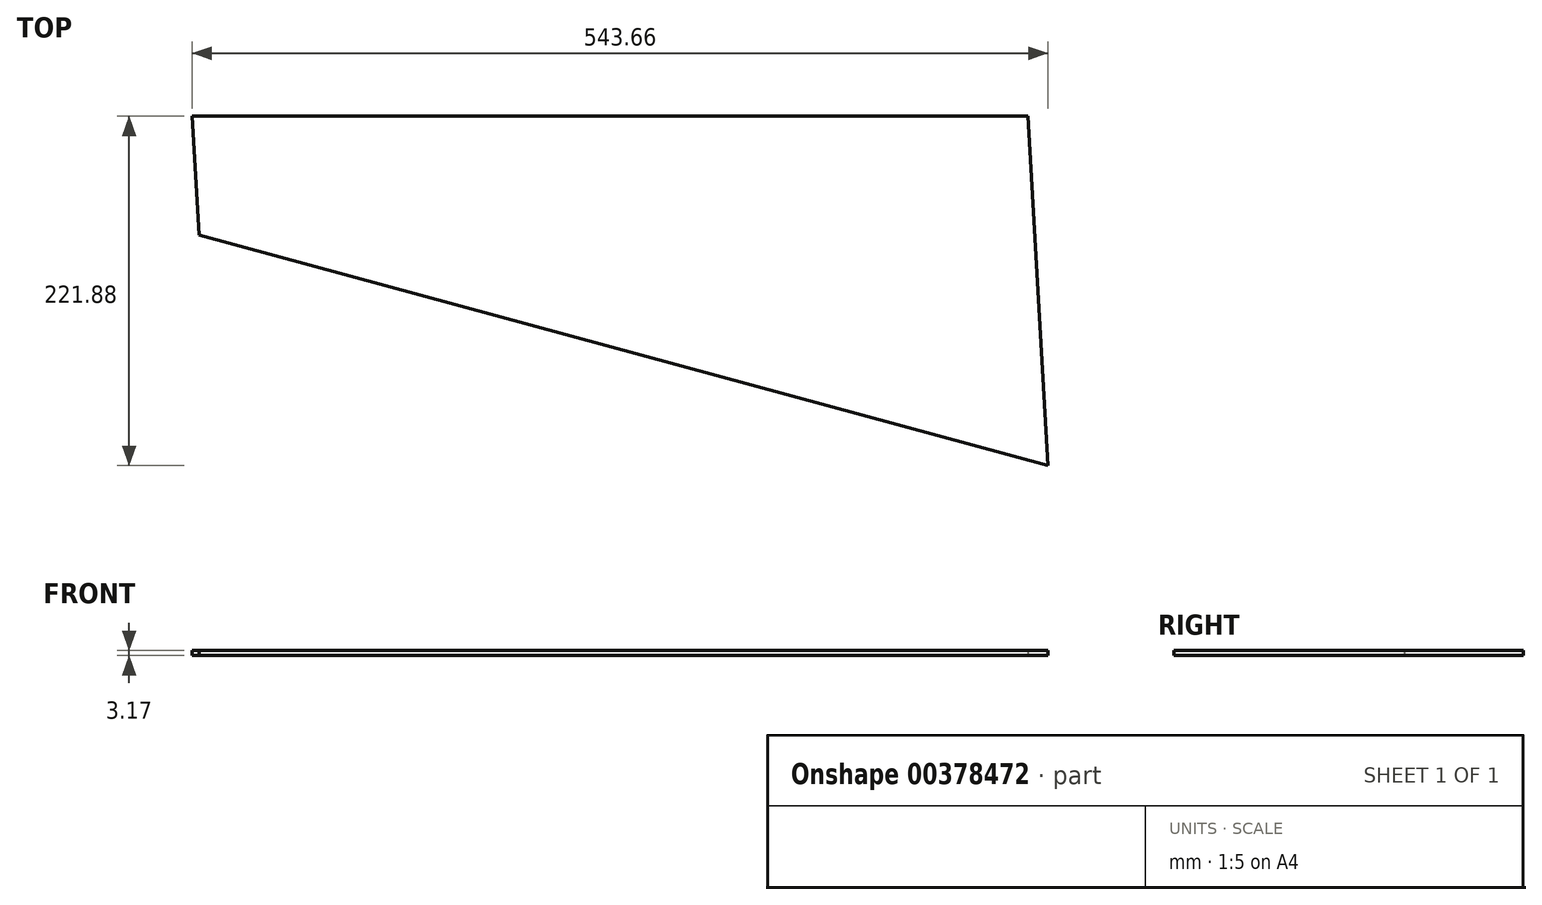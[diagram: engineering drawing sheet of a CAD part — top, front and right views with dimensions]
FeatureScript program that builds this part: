
annotation { "Feature Type Name" : "Feature", "Feature Type Description" : "" }
export const myFeature = defineFeature(function(context is Context, id is Id, definition is map)
    precondition{}
    {
        {
            var Q0;
            Q0=qCreatedBy(makeId("Top.planeOp"),FACE);
            var sketch = newSketch(context, id + "F0", { "sketchPlane" : qUnion([Q0])});
            skLineSegment(sketch, "E0", {"start": v(0, 0) * mm, "end": v(12.85, -221.88) * mm});
            skLineSegment(sketch, "E1", {"start": v(12.85, -221.88) * mm, "end": v(-526.44, -75.51) * mm});
            skLineSegment(sketch, "E2", {"start": v(-526.44, -75.51) * mm, "end": v(-530.81, 0) * mm});
            skLineSegment(sketch, "E3", {"start": v(-530.81, 0) * mm, "end": v(0, 0) * mm});
            skSolve(sketch);
        }
        {
            var Q0;
            Q0 = qSketchRegion(id + "F0", true);
            extrude(context, id + "F1", {"entities" : qUnion([Q0]), "depth" : 3.17 * mm});
        }
    });
